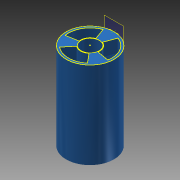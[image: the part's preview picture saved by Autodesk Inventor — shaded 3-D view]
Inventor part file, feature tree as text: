
AUTODESK INVENTOR PART (.ipt)
format: ipt  version: 2013 (Build 170138000, 138)  size: 194,560 bytes
history: native  units: mm
features: sketch x9, extrude x6, other x2, thread x2, hole x1
ambient origin geometry x8: Origin, YZ Plane, XZ Plane, XY Plane, X Axis, Y Axis, Z Axis, Center Point
feature tree (20):
  other  "ソリッド1"
  extrude  "押し出し1"  Depth=55.0mm
  extrude  "押し出し2"  Depth=100.0mm TaperAngle=0.0deg
  extrude  "押し出し3"  Depth=50.0mm
  extrude  "押し出し4"  Depth=97.0mm TaperAngle=0.0deg
  extrude  "押し出し5"  Depth=21.0mm
  sketch  "スケッチ6"
  other  "作業平面1"
  extrude  "押し出し6"  Depth=22.0mm
  hole  "穴1"  [1 undecoded]
  thread  "ねじ1"
  thread  "ねじ2"
  sketch  "スケッチ10"
  sketch  "スケッチ1"
  sketch  "スケッチ2"
  sketch  "スケッチ3"
  sketch  "スケッチ4"
  sketch  "スケッチ5"
  sketch  "スケッチ8"
  sketch  "スケッチ9"
note: 1 required parameter value undecoded (feature->parameter linkage not recoverable at this tier; creation-order binding heuristic only, values carry confidence <= 0.55)
